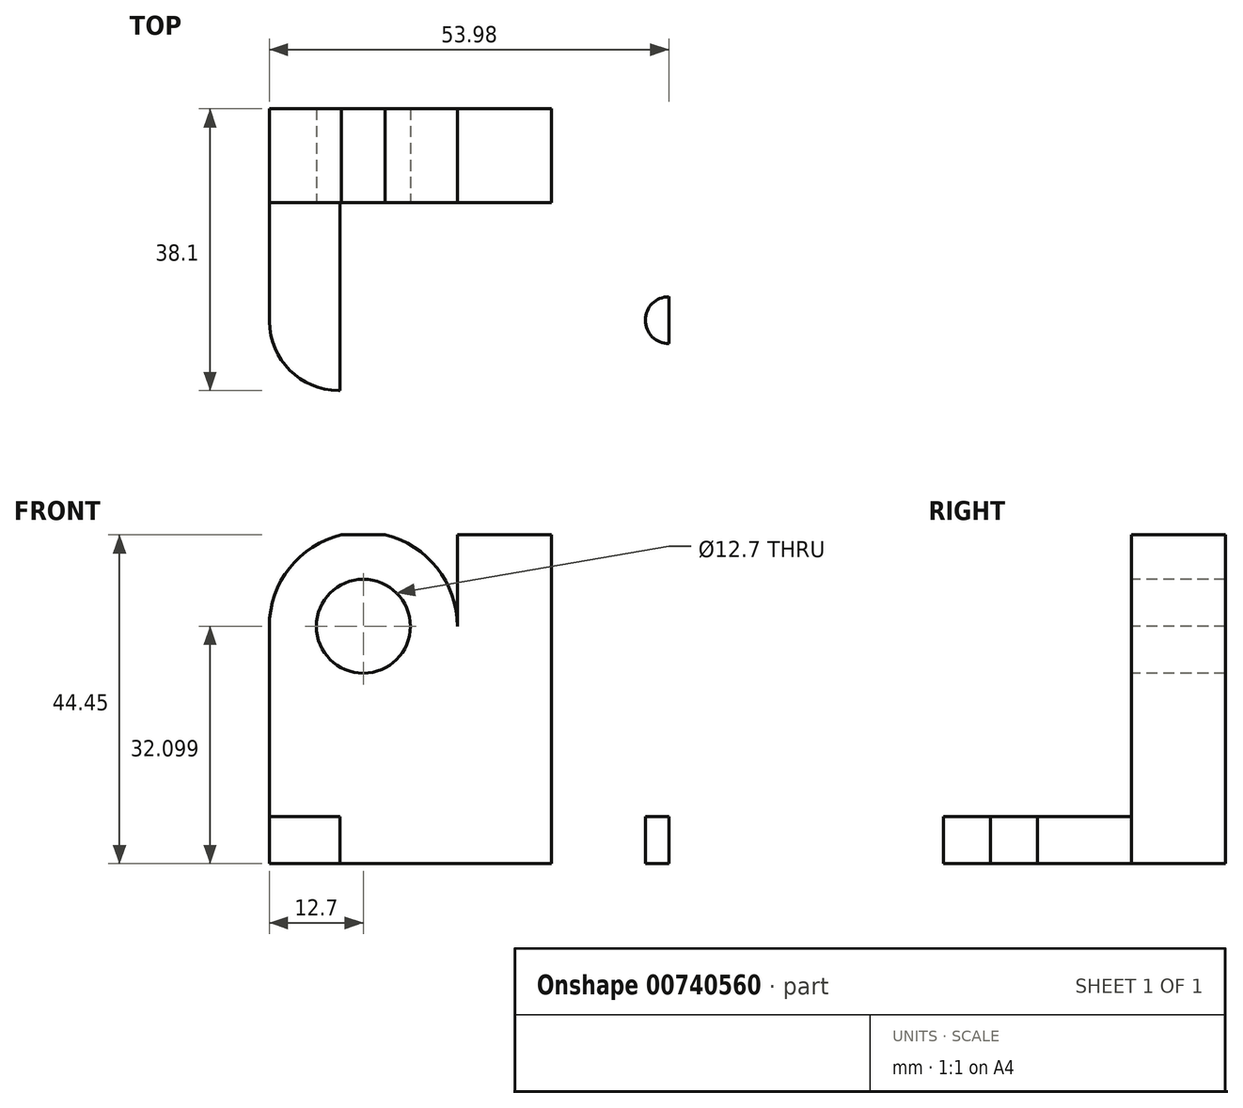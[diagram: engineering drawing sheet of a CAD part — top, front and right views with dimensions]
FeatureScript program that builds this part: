
annotation { "Feature Type Name" : "Feature", "Feature Type Description" : "" }
export const myFeature = defineFeature(function(context is Context, id is Id, definition is map)
    precondition{}
    {
        {
            var Q0;
            Q0=qCreatedBy(makeId("Front.planeOp"),FACE);
            var sketch = newSketch(context, id + "F0", { "sketchPlane" : qUnion([Q0])});
            skLineSegment(sketch, "E0", {"start": v(0, 0) * mm, "end": v(63.5, 0) * mm});
            skLineSegment(sketch, "E1", {"start": v(63.5, 0) * mm, "end": v(63.5, 6.35) * mm});
            skLineSegment(sketch, "E2", {"start": v(63.5, 6.35) * mm, "end": v(38.1, 6.35) * mm});
            skLineSegment(sketch, "E3", {"start": v(38.1, 6.35) * mm, "end": v(38.1, 44.45) * mm});
            skLineSegment(sketch, "E4", {"start": v(38.1, 44.45) * mm, "end": v(0, 44.45) * mm});
            skLineSegment(sketch, "E5", {"start": v(0, 44.45) * mm, "end": v(0, 0) * mm});
            skSolve(sketch);
        }
        {
            var Q0;
            Q0 = qSketchRegion(id + "F0", true);
            extrude(context, id + "F1", {"entities" : qUnion([Q0]), "depth" : 38.1 * mm, "offsetDistance" : 25.4 * mm});
        }
        {
            var Q0;
            Q0=makeQuery(id+"F1.opExtrude","CAP_FACE",FACE,{"disambiguationData":[OSD([sQuery(id+"F0.wireOp",EDGE,"E0"),sQuery(id+"F0.wireOp",EDGE,"E1"),sQuery(id+"F0.wireOp",EDGE,"E2"),sQuery(id+"F0.wireOp",EDGE,"E3"),sQuery(id+"F0.wireOp",EDGE,"E4"),sQuery(id+"F0.wireOp",EDGE,"E5")])],"isStart":false});
            var sketch = newSketch(context, id + "F2", { "sketchPlane" : qUnion([Q0])});
            skLineSegment(sketch, "E6", {"start": v(25.4, 44.45) * mm, "end": v(25.4, 0) * mm});
            skLineSegment(sketch, "E7", {"start": v(38.1, 6.35) * mm, "end": v(0, 6.35) * mm});
            skArc(sketch, "E8", {"start": v(25.4, 19.4) * mm, "mid": v(29, 10.2) * mm, "end": v(38.1, 6.35) * mm});
            skLineSegment(sketch, "E9", {"start": v(25.4, 19.4) * mm, "end": v(25.4, 32.1) * mm});
            skArc(sketch, "E10", {"start": v(25.4, 32.1) * mm, "mid": v(12.7, 44.8) * mm, "end": v(0, 32.1) * mm});
            skLineSegment(sketch, "E11", {"start": v(25.4, 32.1) * mm, "end": v(0, 32.1) * mm});
            skCircle(sketch, "E12", {"center": v(12.7, 32.1) * mm, "radius": 6.35 * mm});
            skSolve(sketch);
        }
        {
            var Q0;
            {var subQ0=sQuery(id+"F2.wireOp",EDGE,"E9");Q0=makeQuery(id+"F2.imprint","IMPRINT",FACE,{"disambiguationData":[TD([[makeQuery(id+"F2.imprint","IMPRINT",EDGE,{"derivedFrom":subQ0}),-1.0]])]});}
            var Q1;
            {var subQ0=sQuery(id+"F2.wireOp",EDGE,"E6");var subQ1=makeQuery(id+"F1.opExtrude","CAP_EDGE",EDGE,{"disambiguationData":[OSD([sQuery(id+"F0.wireOp",EDGE,"E4")])],"isStart":false});var subQ2=makeQuery(id+"F2.imprint","INTERSECT",VERTEX,{"derivedFrom":[subQ1,subQ0]});Q1=makeQuery(id+"F2.imprint","IMPRINT",FACE,{"disambiguationData":[TD([[makeQuery(id+"F2.imprint","IMPRINT",EDGE,{"disambiguationData":[TD([[subQ2,-1.0]])],"derivedFrom":subQ1}),1.0]])]});}
            var Q2;
            {var subQ0=sQuery(id+"F2.wireOp",EDGE,"E12");var subQ1=sQuery(id+"F2.wireOp",EDGE,"E11");var subQ2=makeQuery(id+"F2.imprint","INTERSECT",VERTEX,{"disambiguationData":[OD(0.0)],"derivedFrom":[subQ1,subQ0]});Q2=makeQuery(id+"F2.imprint","IMPRINT",FACE,{"disambiguationData":[TD([[makeQuery(id+"F2.imprint","IMPRINT",EDGE,{"disambiguationData":[TD([[subQ2,-1.0]])],"derivedFrom":subQ1}),1.0]])]});}
            var Q3;
            {var subQ0=sQuery(id+"F2.wireOp",EDGE,"E12");var subQ1=sQuery(id+"F2.wireOp",EDGE,"E11");var subQ2=makeQuery(id+"F2.imprint","INTERSECT",VERTEX,{"disambiguationData":[OD(0.0)],"derivedFrom":[subQ1,subQ0]});Q3=makeQuery(id+"F2.imprint","IMPRINT",FACE,{"disambiguationData":[TD([[makeQuery(id+"F2.imprint","IMPRINT",EDGE,{"disambiguationData":[TD([[subQ2,-1.0]])],"derivedFrom":subQ1}),-1.0]])]});}
            var Q4;
            {var subQ1=makeQuery(id+"F1.opExtrude","CAP_EDGE",EDGE,{"disambiguationData":[OSD([sQuery(id+"F0.wireOp",EDGE,"E5")])],"isStart":false});var subQ3=makeQuery(id+"F1.opExtrude","CAP_EDGE",EDGE,{"disambiguationData":[OSD([sQuery(id+"F0.wireOp",EDGE,"E4")])],"isStart":false});var subQ5=makeQuery(id+"F2.imprint","INTERSECT",VERTEX,{"derivedFrom":[subQ3,subQ1]});Q4=makeQuery(id+"F2.imprint","IMPRINT",FACE,{"disambiguationData":[TD([[makeQuery(id+"F2.imprint","IMPRINT",EDGE,{"disambiguationData":[TD([[subQ5,1.0]])],"derivedFrom":subQ3}),1.0]])]});}
            extrude(context, id + "F3", {"entities" : qUnion([Q0, Q1, Q2, Q3, Q4]), "operationType" : NewBodyOperationType.REMOVE, "endBound" : BoundingType.THROUGH_ALL, "oppositeDirection" : true, "depth" : 25.4 * mm, "offsetDistance" : 25.4 * mm});
        }
        {
            var Q0;
            Q0=makeQuery(id+"F1.opExtrude","CAP_FACE",FACE,{"disambiguationData":[OSD([sQuery(id+"F0.wireOp",EDGE,"E0"),sQuery(id+"F0.wireOp",EDGE,"E1"),sQuery(id+"F0.wireOp",EDGE,"E2"),sQuery(id+"F0.wireOp",EDGE,"E3"),sQuery(id+"F0.wireOp",EDGE,"E4"),sQuery(id+"F0.wireOp",EDGE,"E5")])],"isStart":false});
            var sketch = newSketch(context, id + "F4", { "sketchPlane" : qUnion([Q0])});
            skLineSegment(sketch, "E13", {"start": v(38.1, 6.35) * mm, "end": v(0, 6.35) * mm});
            skLineSegment(sketch, "E14", {"start": v(0, 6.35) * mm, "end": v(0, 32.1) * mm});
            skLineSegment(sketch, "E15", {"start": v(25.4, 32.1) * mm, "end": v(25.4, 18.7) * mm});
            skArc(sketch, "E16", {"start": v(25.4, 32.1) * mm, "mid": v(12.7, 44.8) * mm, "end": v(0, 32.1) * mm});
            skSolve(sketch);
        }
        {
            var Q0;
            {var subQ5=sQuery(id+"F4.wireOp",EDGE,"E14");Q0=makeQuery(id+"F4.imprint","IMPRINT",FACE,{"disambiguationData":[TD([[makeQuery(id+"F4.imprint","IMPRINT",EDGE,{"derivedFrom":subQ5}),1.0]])]});}
            extrude(context, id + "F5", {"entities" : qUnion([Q0]), "operationType" : NewBodyOperationType.REMOVE, "oppositeDirection" : true, "depth" : 25.4 * mm, "offsetDistance" : 25.4 * mm});
        }
        {
            var Q0;
            Q0=makeQuery(id+"F5.boolean.opBoolean","MERGE",FACE,{"derivedFrom":[makeQuery(id+"F1.opExtrude","SWEPT_FACE",FACE,{"disambiguationData":[OSD([sQuery(id+"F0.wireOp",EDGE,"E2")])]}),makeQuery(id+"F5.opExtrude","SWEPT_FACE",FACE,{"disambiguationData":[OSD([sQuery(id+"F4.wireOp",EDGE,"E13")])]})]});
            var sketch = newSketch(context, id + "F6", { "sketchPlane" : qUnion([Q0])});
            skLineSegment(sketch, "E17", {"start": v(0, -28.58) * mm, "end": v(63.5, -28.57) * mm});
            skLineSegment(sketch, "E18", {"start": v(9.53, -38.1) * mm, "end": v(9.52, -12.7) * mm});
            skLineSegment(sketch, "E19", {"start": v(53.98, -38.1) * mm, "end": v(53.98, 0) * mm});
            skCircle(sketch, "E20", {"center": v(53.98, -28.58) * mm, "radius": 3.18 * mm});
            skCircle(sketch, "E21", {"center": v(9.52, -28.58) * mm, "radius": 3.18 * mm});
            skArc(sketch, "E22", {"start": v(0, -28.58) * mm, "mid": v(2.76, -35.34) * mm, "end": v(9.53, -38.1) * mm});
            skArc(sketch, "E23", {"start": v(53.98, -38.1) * mm, "mid": v(60.73, -35.33) * mm, "end": v(63.5, -28.57) * mm});
            skSolve(sketch);
        }
        {
            var Q0;
            {var subQ0=sQuery(id+"F6.wireOp",EDGE,"E21");var subQ1=sQuery(id+"F6.wireOp",EDGE,"E17");var subQ2=makeQuery(id+"F6.imprint","INTERSECT",VERTEX,{"disambiguationData":[OD(0.0)],"derivedFrom":[subQ1,subQ0]});Q0=makeQuery(id+"F6.imprint","IMPRINT",FACE,{"disambiguationData":[TD([[makeQuery(id+"F6.imprint","IMPRINT",EDGE,{"disambiguationData":[TD([[subQ2,-1.0]])],"derivedFrom":subQ1}),-1.0]])]});}
            var Q1;
            {var subQ0=sQuery(id+"F6.wireOp",EDGE,"E21");var subQ1=sQuery(id+"F6.wireOp",EDGE,"E17");var subQ2=makeQuery(id+"F6.imprint","INTERSECT",VERTEX,{"disambiguationData":[OD(0.0)],"derivedFrom":[subQ1,subQ0]});Q1=makeQuery(id+"F6.imprint","IMPRINT",FACE,{"disambiguationData":[TD([[makeQuery(id+"F6.imprint","IMPRINT",EDGE,{"disambiguationData":[TD([[subQ2,-1.0]])],"derivedFrom":subQ1}),1.0]])]});}
            var Q2;
            {var subQ0=sQuery(id+"F6.wireOp",EDGE,"E18");var subQ1=sQuery(id+"F6.wireOp",EDGE,"E17");var subQ2=makeQuery(id+"F6.imprint","INTERSECT",VERTEX,{"derivedFrom":[subQ1,subQ0]});Q2=makeQuery(id+"F6.imprint","IMPRINT",FACE,{"disambiguationData":[TD([[makeQuery(id+"F6.imprint","IMPRINT",EDGE,{"disambiguationData":[TD([[subQ2,-1.0]])],"derivedFrom":subQ1}),-1.0]])]});}
            var Q3;
            {var subQ0=sQuery(id+"F6.wireOp",EDGE,"E18");var subQ1=sQuery(id+"F6.wireOp",EDGE,"E17");var subQ2=makeQuery(id+"F6.imprint","INTERSECT",VERTEX,{"derivedFrom":[subQ1,subQ0]});Q3=makeQuery(id+"F6.imprint","IMPRINT",FACE,{"disambiguationData":[TD([[makeQuery(id+"F6.imprint","IMPRINT",EDGE,{"disambiguationData":[TD([[subQ2,-1.0]])],"derivedFrom":subQ1}),1.0]])]});}
            var Q4;
            {var subQ0=sQuery(id+"F6.wireOp",EDGE,"E20");var subQ1=sQuery(id+"F6.wireOp",EDGE,"E17");var subQ2=makeQuery(id+"F6.imprint","INTERSECT",VERTEX,{"disambiguationData":[OD(0.0)],"derivedFrom":[subQ1,subQ0]});Q4=makeQuery(id+"F6.imprint","IMPRINT",FACE,{"disambiguationData":[TD([[makeQuery(id+"F6.imprint","IMPRINT",EDGE,{"disambiguationData":[TD([[subQ2,-1.0]])],"derivedFrom":subQ1}),-1.0]])]});}
            var Q5;
            {var subQ0=sQuery(id+"F6.wireOp",EDGE,"E20");var subQ1=sQuery(id+"F6.wireOp",EDGE,"E17");var subQ2=makeQuery(id+"F6.imprint","INTERSECT",VERTEX,{"disambiguationData":[OD(0.0)],"derivedFrom":[subQ1,subQ0]});Q5=makeQuery(id+"F6.imprint","IMPRINT",FACE,{"disambiguationData":[TD([[makeQuery(id+"F6.imprint","IMPRINT",EDGE,{"disambiguationData":[TD([[subQ2,-1.0]])],"derivedFrom":subQ1}),1.0]])]});}
            var Q6;
            {var subQ0=sQuery(id+"F6.wireOp",EDGE,"E19");var subQ1=sQuery(id+"F6.wireOp",EDGE,"E17");var subQ2=makeQuery(id+"F6.imprint","INTERSECT",VERTEX,{"derivedFrom":[subQ1,subQ0]});Q6=makeQuery(id+"F6.imprint","IMPRINT",FACE,{"disambiguationData":[TD([[makeQuery(id+"F6.imprint","IMPRINT",EDGE,{"disambiguationData":[TD([[subQ2,-1.0]])],"derivedFrom":subQ1}),-1.0]])]});}
            var Q7;
            {var subQ0=sQuery(id+"F6.wireOp",EDGE,"E19");var subQ1=sQuery(id+"F6.wireOp",EDGE,"E17");var subQ2=makeQuery(id+"F6.imprint","INTERSECT",VERTEX,{"derivedFrom":[subQ1,subQ0]});Q7=makeQuery(id+"F6.imprint","IMPRINT",FACE,{"disambiguationData":[TD([[makeQuery(id+"F6.imprint","IMPRINT",EDGE,{"disambiguationData":[TD([[subQ2,-1.0]])],"derivedFrom":subQ1}),1.0]])]});}
            var Q8;
            {var subQ0=sQuery(id+"F6.wireOp",EDGE,"E22");var subQ1=makeQuery(id+"F5.boolean.opBoolean","COPY",EDGE,{"derivedFrom":makeQuery(id+"F5.opExtrude","SWEPT_EDGE",EDGE,{"disambiguationData":[OSD([sQuery(id+"F0.wireOp",EDGE,"E5"),sQuery(id+"F4.wireOp",EDGE,"E13"),sQuery(id+"F4.wireOp",EDGE,"E14")])]})});var subQ3=makeQuery(id+"F6.imprint","INTERSECT",VERTEX,{"derivedFrom":[subQ1,subQ0]});Q8=makeQuery(id+"F6.imprint","IMPRINT",FACE,{"disambiguationData":[TD([[makeQuery(id+"F6.imprint","IMPRINT",EDGE,{"disambiguationData":[TD([[subQ3,1.0]])],"derivedFrom":subQ0}),1.0]])]});}
            var Q9;
            {var subQ0=sQuery(id+"F6.wireOp",EDGE,"E22");var subQ1=makeQuery(id+"F5.boolean.opBoolean","MERGE",EDGE,{"derivedFrom":[makeQuery(id+"F1.opExtrude","CAP_EDGE",EDGE,{"disambiguationData":[OSD([sQuery(id+"F0.wireOp",EDGE,"E2")])],"isStart":false}),makeQuery(id+"F5.opExtrude","CAP_EDGE",EDGE,{"disambiguationData":[OSD([sQuery(id+"F4.wireOp",EDGE,"E13")])],"isStart":true})]});var subQ3=makeQuery(id+"F6.imprint","INTERSECT",VERTEX,{"derivedFrom":[subQ1,subQ0]});Q9=makeQuery(id+"F6.imprint","IMPRINT",FACE,{"disambiguationData":[TD([[makeQuery(id+"F6.imprint","IMPRINT",EDGE,{"disambiguationData":[TD([[subQ3,-1.0]])],"derivedFrom":subQ0}),1.0]])]});}
            var Q10;
            {var subQ0=sQuery(id+"F6.wireOp",EDGE,"E23");var subQ1=makeQuery(id+"F5.boolean.opBoolean","MERGE",EDGE,{"derivedFrom":[makeQuery(id+"F1.opExtrude","CAP_EDGE",EDGE,{"disambiguationData":[OSD([sQuery(id+"F0.wireOp",EDGE,"E2")])],"isStart":false}),makeQuery(id+"F5.opExtrude","CAP_EDGE",EDGE,{"disambiguationData":[OSD([sQuery(id+"F4.wireOp",EDGE,"E13")])],"isStart":true})]});var subQ3=makeQuery(id+"F6.imprint","INTERSECT",VERTEX,{"derivedFrom":[subQ1,subQ0]});Q10=makeQuery(id+"F6.imprint","IMPRINT",FACE,{"disambiguationData":[TD([[makeQuery(id+"F6.imprint","IMPRINT",EDGE,{"disambiguationData":[TD([[subQ3,1.0]])],"derivedFrom":subQ0}),1.0]])]});}
            var Q11;
            {var subQ0=sQuery(id+"F6.wireOp",EDGE,"E23");var subQ1=makeQuery(id+"F1.opExtrude","SWEPT_EDGE",EDGE,{"disambiguationData":[OSD([sQuery(id+"F0.wireOp",EDGE,"E1"),sQuery(id+"F0.wireOp",EDGE,"E2")])]});var subQ3=makeQuery(id+"F6.imprint","INTERSECT",VERTEX,{"derivedFrom":[subQ1,subQ0]});Q11=makeQuery(id+"F6.imprint","IMPRINT",FACE,{"disambiguationData":[TD([[makeQuery(id+"F6.imprint","IMPRINT",EDGE,{"disambiguationData":[TD([[subQ3,-1.0]])],"derivedFrom":subQ0}),1.0]])]});}
            var Q12;
            {var subQ0=sQuery(id+"F6.wireOp",EDGE,"E22");var subQ1=sQuery(id+"F4.wireOp",EDGE,"E13");var subQ4=makeQuery(id+"F5.boolean.opBoolean","MERGE",EDGE,{"derivedFrom":[makeQuery(id+"F1.opExtrude","CAP_EDGE",EDGE,{"disambiguationData":[OSD([sQuery(id+"F0.wireOp",EDGE,"E2")])],"isStart":false}),makeQuery(id+"F5.opExtrude","CAP_EDGE",EDGE,{"disambiguationData":[OSD([subQ1])],"isStart":true})]});var subQ5=makeQuery(id+"F6.imprint","INTERSECT",VERTEX,{"derivedFrom":[subQ4,subQ0]});Q12=makeQuery(id+"F6.imprint","IMPRINT",FACE,{"disambiguationData":[TD([[makeQuery(id+"F6.imprint","IMPRINT",EDGE,{"disambiguationData":[TD([[subQ5,1.0]])],"derivedFrom":subQ0}),-1.0]])]});}
            var Q13;
            {var subQ0=sQuery(id+"F6.wireOp",EDGE,"E23");var subQ1=sQuery(id+"F0.wireOp",EDGE,"E2");var subQ2=makeQuery(id+"F5.boolean.opBoolean","MERGE",EDGE,{"derivedFrom":[makeQuery(id+"F1.opExtrude","CAP_EDGE",EDGE,{"disambiguationData":[OSD([subQ1])],"isStart":false}),makeQuery(id+"F5.opExtrude","CAP_EDGE",EDGE,{"disambiguationData":[OSD([sQuery(id+"F4.wireOp",EDGE,"E13")])],"isStart":true})]});var subQ3=makeQuery(id+"F6.imprint","INTERSECT",VERTEX,{"derivedFrom":[subQ2,subQ0]});Q13=makeQuery(id+"F6.imprint","IMPRINT",FACE,{"disambiguationData":[TD([[makeQuery(id+"F6.imprint","IMPRINT",EDGE,{"disambiguationData":[TD([[subQ3,-1.0]])],"derivedFrom":subQ0}),-1.0]])]});}
            extrude(context, id + "F7", {"entities" : qUnion([Q0, Q1, Q2, Q3, Q4, Q5, Q6, Q7, Q8, Q9, Q10, Q11, Q12, Q13]), "operationType" : NewBodyOperationType.REMOVE, "endBound" : BoundingType.THROUGH_ALL, "oppositeDirection" : true, "depth" : 25.4 * mm, "offsetDistance" : 25.4 * mm});
        }
        {
            var Q0;
            Q0=makeQuery(id+"F5.boolean.opBoolean","MERGE",FACE,{"derivedFrom":[makeQuery(id+"F1.opExtrude","SWEPT_FACE",FACE,{"disambiguationData":[OSD([sQuery(id+"F0.wireOp",EDGE,"E2")])]}),makeQuery(id+"F5.opExtrude","SWEPT_FACE",FACE,{"disambiguationData":[OSD([sQuery(id+"F4.wireOp",EDGE,"E13")])]})]});
            var sketch = newSketch(context, id + "F8", { "sketchPlane" : qUnion([Q0])});
            skCircle(sketch, "E24", {"center": v(54.26, -6.78) * mm, "radius": 3.18 * mm});
            skSolve(sketch);
        }
        {
            var Q0;
            Q0 = qSketchRegion(id + "F8", true);
            extrude(context, id + "F9", {"entities" : qUnion([Q0]), "operationType" : NewBodyOperationType.REMOVE, "endBound" : BoundingType.THROUGH_ALL, "depth" : 25.4 * mm, "offsetDistance" : 25.4 * mm});
        }
        {
            var Q0;
            Q0=makeQuery(id+"F5.boolean.opBoolean","MERGE",FACE,{"derivedFrom":[makeQuery(id+"F1.opExtrude","SWEPT_FACE",FACE,{"disambiguationData":[OSD([sQuery(id+"F0.wireOp",EDGE,"E2")])]}),makeQuery(id+"F5.opExtrude","SWEPT_FACE",FACE,{"disambiguationData":[OSD([sQuery(id+"F4.wireOp",EDGE,"E13")])]})]});
            var sketch = newSketch(context, id + "F10", { "sketchPlane" : qUnion([Q0])});
            skCircle(sketch, "E25", {"center": v(54.27, -6.35) * mm, "radius": 3.18 * mm});
            skPoint(sketch, "E25.centerSnap0", {"position": v(38.1, -6.35) * mm});
            skSolve(sketch);
        }
        {
            var Q0;
            Q0 = qSketchRegion(id + "F10", true);
            extrude(context, id + "F11", {"entities" : qUnion([Q0]), "operationType" : NewBodyOperationType.REMOVE, "endBound" : BoundingType.THROUGH_ALL, "oppositeDirection" : true, "depth" : 25.4 * mm, "offsetDistance" : 25.4 * mm});
        }
    });
